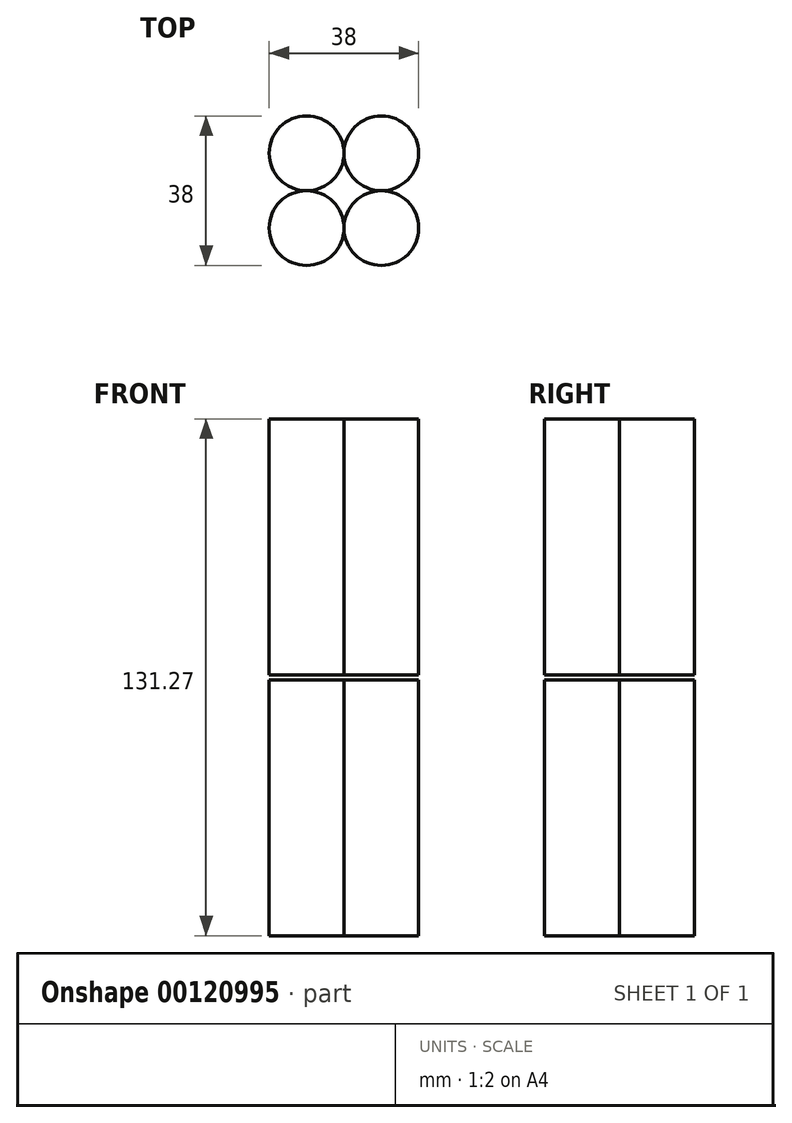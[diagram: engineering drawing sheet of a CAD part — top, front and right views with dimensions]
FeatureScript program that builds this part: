
annotation { "Feature Type Name" : "Feature", "Feature Type Description" : "" }
export const myFeature = defineFeature(function(context is Context, id is Id, definition is map)
    precondition{}
    {
        {
            var Q0;
            Q0=qCreatedBy(makeId("Top.planeOp"),FACE);
            var sketch = newSketch(context, id + "F0", { "sketchPlane" : qUnion([Q0])});
            skCircle(sketch, "E0", {"center": v(-9.5, 9.5) * mm, "radius": 9.5 * mm});
            skCircle(sketch, "E1", {"center": v(9.5, 9.5) * mm, "radius": 9.5 * mm});
            skCircle(sketch, "E2", {"center": v(-9.5, -9.5) * mm, "radius": 9.5 * mm});
            skCircle(sketch, "E3", {"center": v(9.5, -9.5) * mm, "radius": 9.5 * mm});
            skSolve(sketch);
        }
        {
            var Q0;
            {var subQ0=sQuery(id+"F0.wireOp",EDGE,"E1");var subQ2=makeQuery(id+"F0.imprint","INTERSECT",VERTEX,{"derivedFrom":[sQuery(id+"F0.wireOp",EDGE,"E0"),subQ0]});Q0=makeQuery(id+"F0.imprint","IMPRINT",FACE,{"disambiguationData":[TD([[makeQuery(id+"F0.imprint","IMPRINT",EDGE,{"disambiguationData":[TD([[subQ2,-1.0]])],"derivedFrom":subQ0}),1.0]])]});}
            var Q1;
            {var subQ0=sQuery(id+"F0.wireOp",EDGE,"E3");var subQ2=makeQuery(id+"F0.imprint","INTERSECT",VERTEX,{"derivedFrom":[sQuery(id+"F0.wireOp",EDGE,"E1"),subQ0]});Q1=makeQuery(id+"F0.imprint","IMPRINT",FACE,{"disambiguationData":[TD([[makeQuery(id+"F0.imprint","IMPRINT",EDGE,{"disambiguationData":[TD([[subQ2,-1.0]])],"derivedFrom":subQ0}),1.0]])]});}
            var Q2;
            {var subQ0=sQuery(id+"F0.wireOp",EDGE,"E2");var subQ2=makeQuery(id+"F0.imprint","INTERSECT",VERTEX,{"derivedFrom":[sQuery(id+"F0.wireOp",EDGE,"E0"),subQ0]});Q2=makeQuery(id+"F0.imprint","IMPRINT",FACE,{"disambiguationData":[TD([[makeQuery(id+"F0.imprint","IMPRINT",EDGE,{"disambiguationData":[TD([[subQ2,1.0]])],"derivedFrom":subQ0}),1.0]])]});}
            var Q3;
            {var subQ0=sQuery(id+"F0.wireOp",EDGE,"E0");var subQ2=makeQuery(id+"F0.imprint","INTERSECT",VERTEX,{"derivedFrom":[subQ0,sQuery(id+"F0.wireOp",EDGE,"E1")]});Q3=makeQuery(id+"F0.imprint","IMPRINT",FACE,{"disambiguationData":[TD([[makeQuery(id+"F0.imprint","IMPRINT",EDGE,{"disambiguationData":[TD([[subQ2,-1.0]])],"derivedFrom":subQ0}),1.0]])]});}
            extrude(context, id + "F1", {"entities" : qUnion([Q0, Q1, Q2, Q3]), "depth" : 65 * mm});
        }
        {
            var Q0;
            Q0=makeQuery(id+"F1.opExtrude","CAP_FACE",FACE,{"disambiguationData":[OSD([sQuery(id+"F0.wireOp",EDGE,"E1")])],"isStart":false});
            cPlane(context, id + "F2", {"entities" : qUnion([Q0]), "cplaneType" : CPlaneType.OFFSET, "offset" : 1.27 * mm, "width" : 152.4 * mm, "height" : 152.4 * mm});
        }
        {
            var Q0;
            Q0=qCreatedBy(id+"F2.planeOp",FACE);
            var sketch = newSketch(context, id + "F3", { "sketchPlane" : qUnion([Q0])});
            skCircle(sketch, "E4", {"center": v(-9.5, -9.5) * mm, "radius": 9.5 * mm});
            skCircle(sketch, "E5", {"center": v(9.5, -9.5) * mm, "radius": 9.5 * mm});
            skCircle(sketch, "E6", {"center": v(9.5, 9.5) * mm, "radius": 9.5 * mm});
            skCircle(sketch, "E7", {"center": v(-9.5, 9.5) * mm, "radius": 9.5 * mm});
            skSolve(sketch);
        }
        {
            var Q0;
            {var subQ0=sQuery(id+"F3.wireOp",EDGE,"E6");var subQ2=makeQuery(id+"F3.imprint","INTERSECT",VERTEX,{"derivedFrom":[sQuery(id+"F3.wireOp",EDGE,"E5"),subQ0]});Q0=makeQuery(id+"F3.imprint","IMPRINT",FACE,{"disambiguationData":[TD([[makeQuery(id+"F3.imprint","IMPRINT",EDGE,{"disambiguationData":[TD([[subQ2,1.0]])],"derivedFrom":subQ0}),1.0]])]});}
            var Q1;
            {var subQ0=sQuery(id+"F3.wireOp",EDGE,"E5");var subQ2=makeQuery(id+"F3.imprint","INTERSECT",VERTEX,{"derivedFrom":[sQuery(id+"F3.wireOp",EDGE,"E4"),subQ0]});Q1=makeQuery(id+"F3.imprint","IMPRINT",FACE,{"disambiguationData":[TD([[makeQuery(id+"F3.imprint","IMPRINT",EDGE,{"disambiguationData":[TD([[subQ2,1.0]])],"derivedFrom":subQ0}),1.0]])]});}
            var Q2;
            {var subQ0=sQuery(id+"F3.wireOp",EDGE,"E4");var subQ2=makeQuery(id+"F3.imprint","INTERSECT",VERTEX,{"derivedFrom":[subQ0,sQuery(id+"F3.wireOp",EDGE,"E5")]});Q2=makeQuery(id+"F3.imprint","IMPRINT",FACE,{"disambiguationData":[TD([[makeQuery(id+"F3.imprint","IMPRINT",EDGE,{"disambiguationData":[TD([[subQ2,1.0]])],"derivedFrom":subQ0}),1.0]])]});}
            var Q3;
            {var subQ0=sQuery(id+"F3.wireOp",EDGE,"E7");var subQ2=makeQuery(id+"F3.imprint","INTERSECT",VERTEX,{"derivedFrom":[sQuery(id+"F3.wireOp",EDGE,"E4"),subQ0]});Q3=makeQuery(id+"F3.imprint","IMPRINT",FACE,{"disambiguationData":[TD([[makeQuery(id+"F3.imprint","IMPRINT",EDGE,{"disambiguationData":[TD([[subQ2,1.0]])],"derivedFrom":subQ0}),1.0]])]});}
            var Q4;
            Q4=sQuery(id+"F3.wireOp",EDGE,"E6");
            var Q5;
            Q5=sQuery(id+"F3.wireOp",EDGE,"E5");
            var Q6;
            Q6=sQuery(id+"F3.wireOp",EDGE,"E4");
            var Q7;
            Q7=sQuery(id+"F3.wireOp",EDGE,"E7");
            extrude(context, id + "F4", {"entities" : qUnion([Q0, Q1, Q2, Q3]), "surfaceEntities" : qUnion([Q4, Q5, Q6, Q7]), "depth" : 65 * mm});
        }
        {
            var Q0;
            Q0=makeQuery(id+"F4.opExtrude","CAP_FACE",FACE,{"disambiguationData":[OSD([sQuery(id+"F3.wireOp",EDGE,"E7")])],"isStart":false});
            var sketch = newSketch(context, id + "F5", { "sketchPlane" : qUnion([Q0])});
            skCircle(sketch, "E8", {"center": v(0, 0) * mm, "radius": 22.94 * mm});
            skSolve(sketch);
        }
    });
